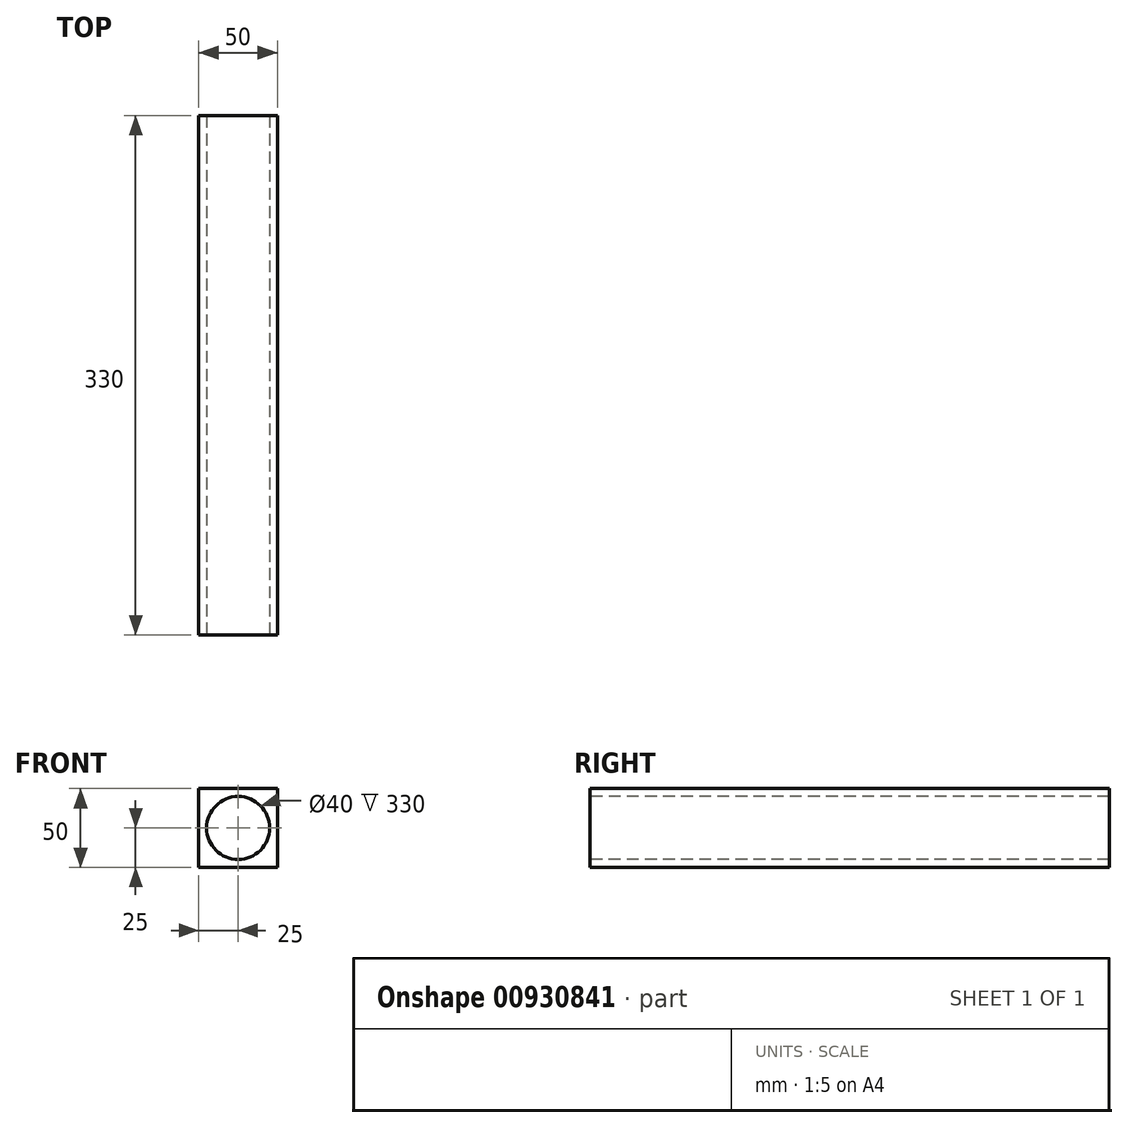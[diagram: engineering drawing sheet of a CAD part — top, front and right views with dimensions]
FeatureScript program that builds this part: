
annotation { "Feature Type Name" : "Feature", "Feature Type Description" : "" }
export const myFeature = defineFeature(function(context is Context, id is Id, definition is map)
    precondition{}
    {
        {
            var Q0;
            Q0=qCreatedBy(makeId("Front.planeOp"),FACE);
            var sketch = newSketch(context, id + "F0", { "sketchPlane" : qUnion([Q0])});
            skCircle(sketch, "E0", {"center": v(0, 0) * mm, "radius": 20 * mm});
            skLineSegment(sketch, "E1.bottom", {"start": v(25, 25) * mm, "end": v(-25, 25) * mm});
            skLineSegment(sketch, "E1.top", {"start": v(25, -25) * mm, "end": v(-25, -25) * mm});
            skLineSegment(sketch, "E1.left", {"start": v(25, 25) * mm, "end": v(25, -25) * mm});
            skLineSegment(sketch, "E1.right", {"start": v(-25, 25) * mm, "end": v(-25, -25) * mm});
            skSolve(sketch);
        }
        {
            var Q0;
            Q0=makeQuery(id+"F0.imprint","IMPRINT",FACE,{"disambiguationData":[TD([[makeQuery(id+"F0.imprint","IMPRINT",EDGE,{"derivedFrom":sQuery(id+"F0.wireOp",EDGE,"E0")}),-1.0]])]});
            extrude(context, id + "F1", {"entities" : qUnion([Q0]), "endBound" : BoundingType.SYMMETRIC, "oppositeDirection" : true, "depth" : 330 * mm, "offsetDistance" : 25 * mm});
        }
    });
